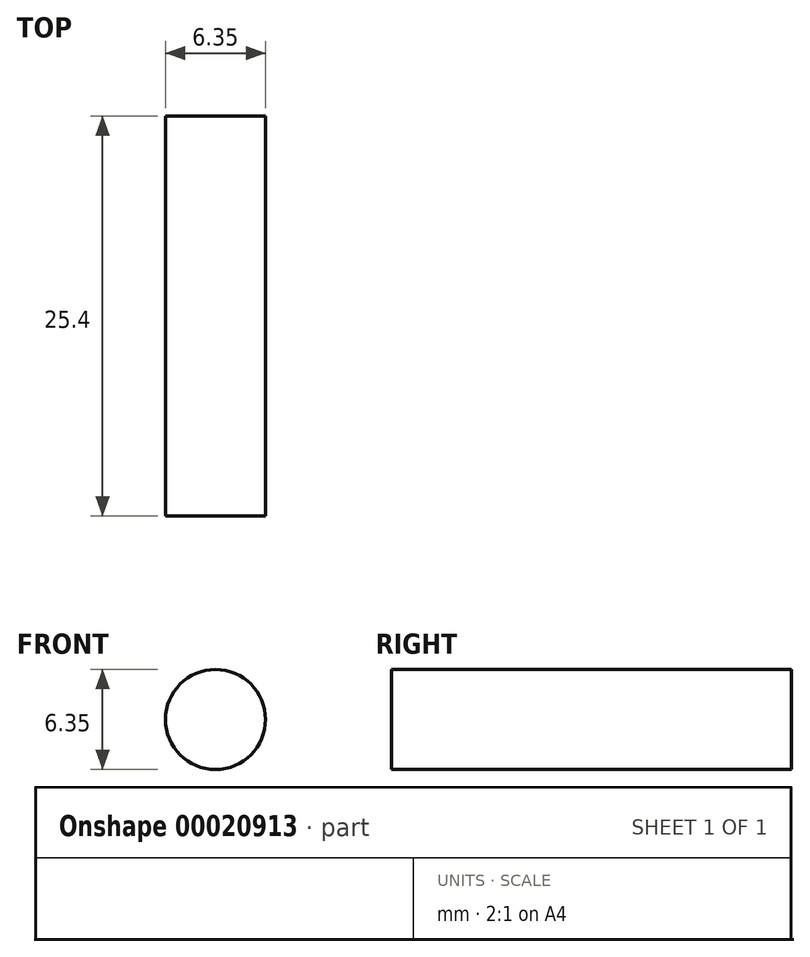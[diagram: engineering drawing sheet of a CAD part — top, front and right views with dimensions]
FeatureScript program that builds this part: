
annotation { "Feature Type Name" : "Feature", "Feature Type Description" : "" }
export const myFeature = defineFeature(function(context is Context, id is Id, definition is map)
    precondition{}
    {
        {
            var Q0;
            Q0=qCreatedBy(makeId("Front.planeOp"),FACE);
            var sketch = newSketch(context, id + "F0", { "sketchPlane" : qUnion([Q0])});
            skCircle(sketch, "E0", {"center": v(-44.92, 21.88) * mm, "radius": 3.18 * mm});
            skSolve(sketch);
        }
        {
            var Q0;
            Q0 = qSketchRegion(id + "F0", true);
            extrude(context, id + "F1", {"entities" : qUnion([Q0]), "depth" : 25.4 * mm});
        }
    });
